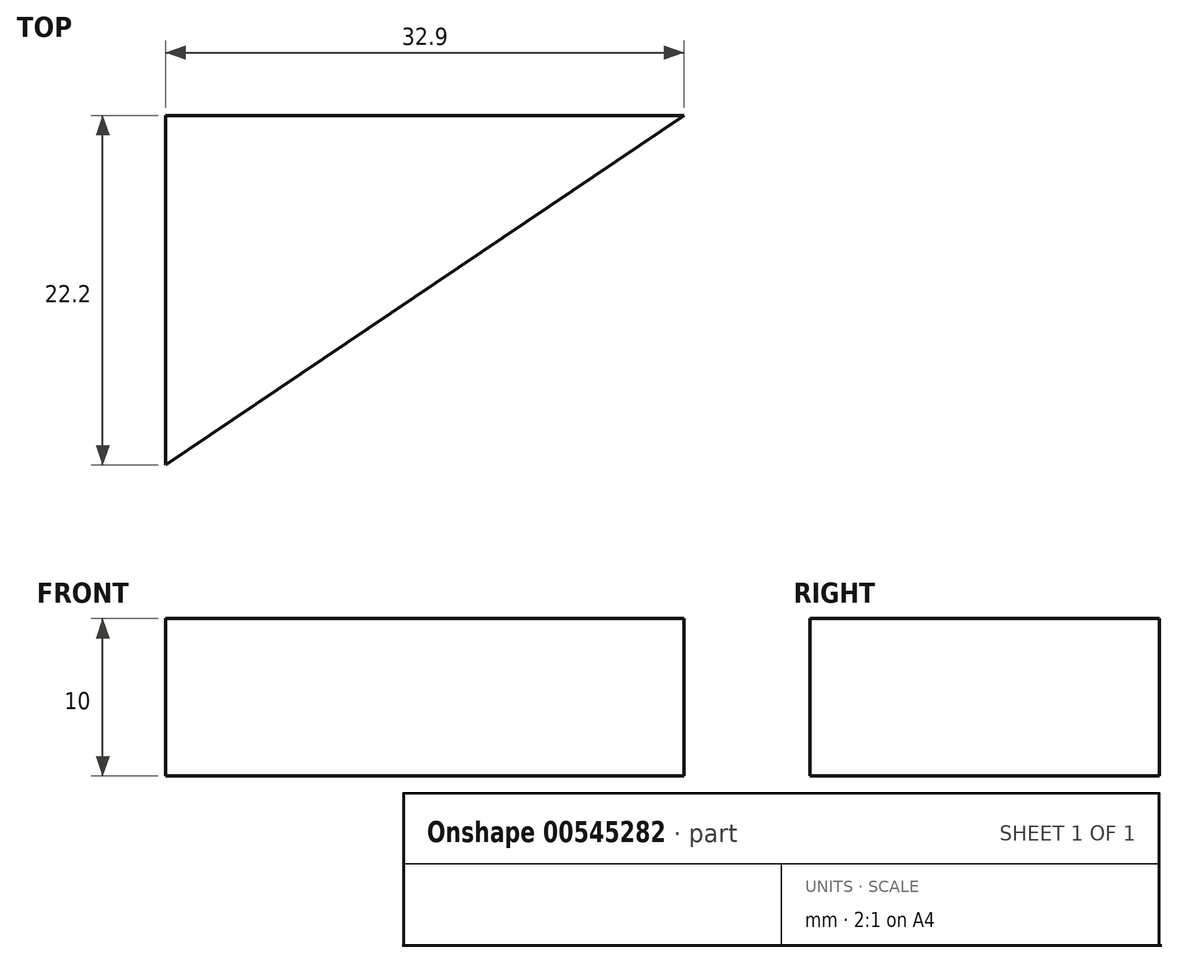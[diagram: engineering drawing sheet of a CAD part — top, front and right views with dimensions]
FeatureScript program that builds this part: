
annotation { "Feature Type Name" : "Feature", "Feature Type Description" : "" }
export const myFeature = defineFeature(function(context is Context, id is Id, definition is map)
    precondition{}
    {
        {
            var Q0;
            Q0=qCreatedBy(makeId("Top.planeOp"),FACE);
            var sketch = newSketch(context, id + "F0", { "sketchPlane" : qUnion([Q0])});
            skLineSegment(sketch, "E0.bottom", {"start": v(0, 0) * mm, "end": v(32.9, 0) * mm});
            skLineSegment(sketch, "E0.top", {"start": v(0, -22.2) * mm, "end": v(32.9, -22.2) * mm});
            skLineSegment(sketch, "E0.left", {"start": v(0, 0) * mm, "end": v(0, -22.2) * mm});
            skLineSegment(sketch, "E0.right", {"start": v(32.9, 0) * mm, "end": v(32.9, -22.2) * mm});
            skSolve(sketch);
        }
        {
            var Q0;
            Q0 = qSketchRegion(id + "F0", true);
            extrude(context, id + "F1", {"entities" : qUnion([Q0]), "depth" : 10 * mm, "offsetDistance" : 25 * mm});
        }
        {
            var Q0;
            Q0=makeQuery(id+"F1.opExtrude","CAP_FACE",FACE,{"disambiguationData":[OSD([sQuery(id+"F0.wireOp",EDGE,"E0.bottom"),sQuery(id+"F0.wireOp",EDGE,"E0.top"),sQuery(id+"F0.wireOp",EDGE,"E0.left"),sQuery(id+"F0.wireOp",EDGE,"E0.right")])],"isStart":false});
            var sketch = newSketch(context, id + "F2", { "sketchPlane" : qUnion([Q0])});
            skLineSegment(sketch, "E1", {"start": v(0, 0) * mm, "end": v(32.9, -22.2) * mm});
            skLineSegment(sketch, "E2", {"start": v(32.9, -22.2) * mm, "end": v(0, -22.2) * mm});
            skLineSegment(sketch, "E3", {"start": v(0, -22.2) * mm, "end": v(32.9, 0) * mm});
            skCircle(sketch, "E4", {"center": v(16.45, -11.1) * mm, "radius": 2 * mm});
            skSolve(sketch);
        }
        {
            var Q0;
            {var subQ0=sQuery(id+"F2.wireOp",EDGE,"E4");var subQ1=sQuery(id+"F2.wireOp",EDGE,"E1");var subQ2=makeQuery(id+"F2.imprint","INTERSECT",VERTEX,{"disambiguationData":[OD(0.0)],"derivedFrom":[subQ1,subQ0]});Q0=makeQuery(id+"F2.imprint","IMPRINT",FACE,{"disambiguationData":[TD([[makeQuery(id+"F2.imprint","IMPRINT",EDGE,{"disambiguationData":[TD([[subQ2,-1.0]])],"derivedFrom":subQ1}),-1.0]])]});}
            var Q1;
            {var subQ0=sQuery(id+"F2.wireOp",EDGE,"E4");var subQ1=sQuery(id+"F2.wireOp",EDGE,"E1");var subQ2=makeQuery(id+"F2.imprint","INTERSECT",VERTEX,{"disambiguationData":[OD(0.0)],"derivedFrom":[subQ1,subQ0]});Q1=makeQuery(id+"F2.imprint","IMPRINT",FACE,{"disambiguationData":[TD([[makeQuery(id+"F2.imprint","IMPRINT",EDGE,{"disambiguationData":[TD([[subQ2,-1.0]])],"derivedFrom":subQ1}),1.0]])]});}
            var Q2;
            {var subQ0=sQuery(id+"F2.wireOp",EDGE,"E3");var subQ1=sQuery(id+"F2.wireOp",EDGE,"E1");var subQ2=makeQuery(id+"F2.imprint","INTERSECT",VERTEX,{"derivedFrom":[subQ1,subQ0]});Q2=makeQuery(id+"F2.imprint","IMPRINT",FACE,{"disambiguationData":[TD([[makeQuery(id+"F2.imprint","IMPRINT",EDGE,{"disambiguationData":[TD([[subQ2,-1.0]])],"derivedFrom":subQ1}),-1.0]])]});}
            var Q3;
            {var subQ0=sQuery(id+"F2.wireOp",EDGE,"E3");var subQ1=sQuery(id+"F2.wireOp",EDGE,"E1");var subQ2=makeQuery(id+"F2.imprint","INTERSECT",VERTEX,{"derivedFrom":[subQ1,subQ0]});Q3=makeQuery(id+"F2.imprint","IMPRINT",FACE,{"disambiguationData":[TD([[makeQuery(id+"F2.imprint","IMPRINT",EDGE,{"disambiguationData":[TD([[subQ2,-1.0]])],"derivedFrom":subQ1}),1.0]])]});}
            extrude(context, id + "F3", {"entities" : qUnion([Q0, Q1, Q2, Q3]), "operationType" : NewBodyOperationType.REMOVE, "oppositeDirection" : true, "depth" : 25 * mm, "offsetDistance" : 25 * mm});
        }
    });
